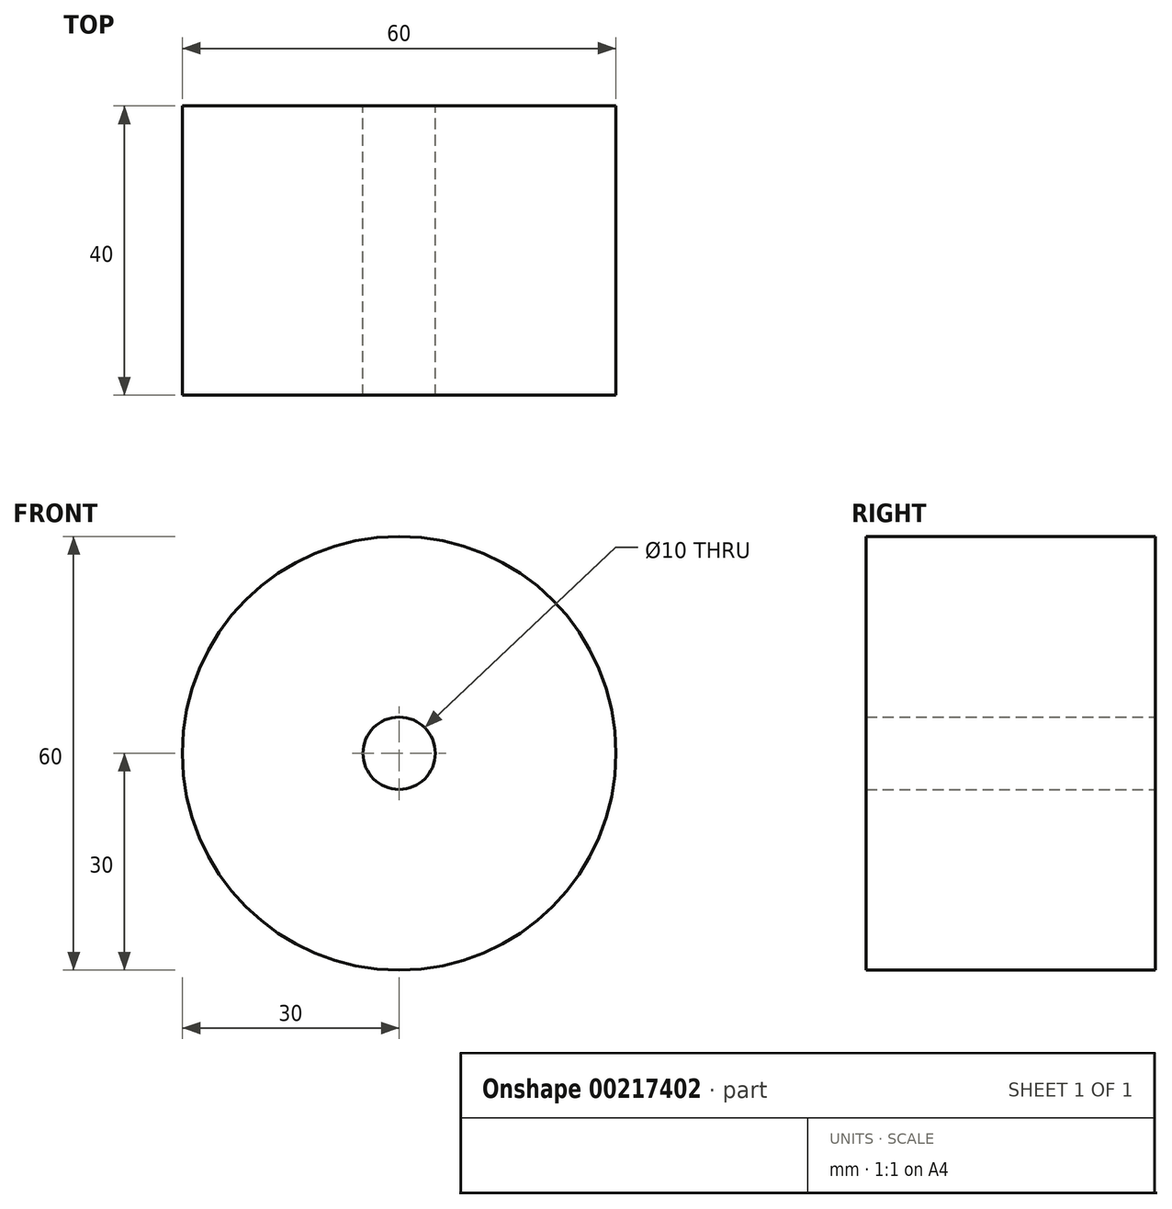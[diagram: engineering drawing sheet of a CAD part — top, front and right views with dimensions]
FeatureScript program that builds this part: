
annotation { "Feature Type Name" : "Feature", "Feature Type Description" : "" }
export const myFeature = defineFeature(function(context is Context, id is Id, definition is map)
    precondition{}
    {
        {
            var Q0;
            Q0=qCreatedBy(makeId("Front.planeOp"),FACE);
            var sketch = newSketch(context, id + "F0", { "sketchPlane" : qUnion([Q0])});
            skCircle(sketch, "E0", {"center": v(0, 0) * mm, "radius": 30 * mm});
            skCircle(sketch, "E1", {"center": v(0, 0) * mm, "radius": 5 * mm});
            skSolve(sketch);
        }
        {
            var Q0;
            Q0=makeQuery(id+"F0.imprint","IMPRINT",FACE,{"disambiguationData":[TD([[makeQuery(id+"F0.imprint","IMPRINT",EDGE,{"derivedFrom":sQuery(id+"F0.wireOp",EDGE,"E0")}),1.0]])]});
            extrude(context, id + "F1", {"entities" : qUnion([Q0]), "endBound" : BoundingType.SYMMETRIC, "depth" : 40 * mm});
        }
    });
